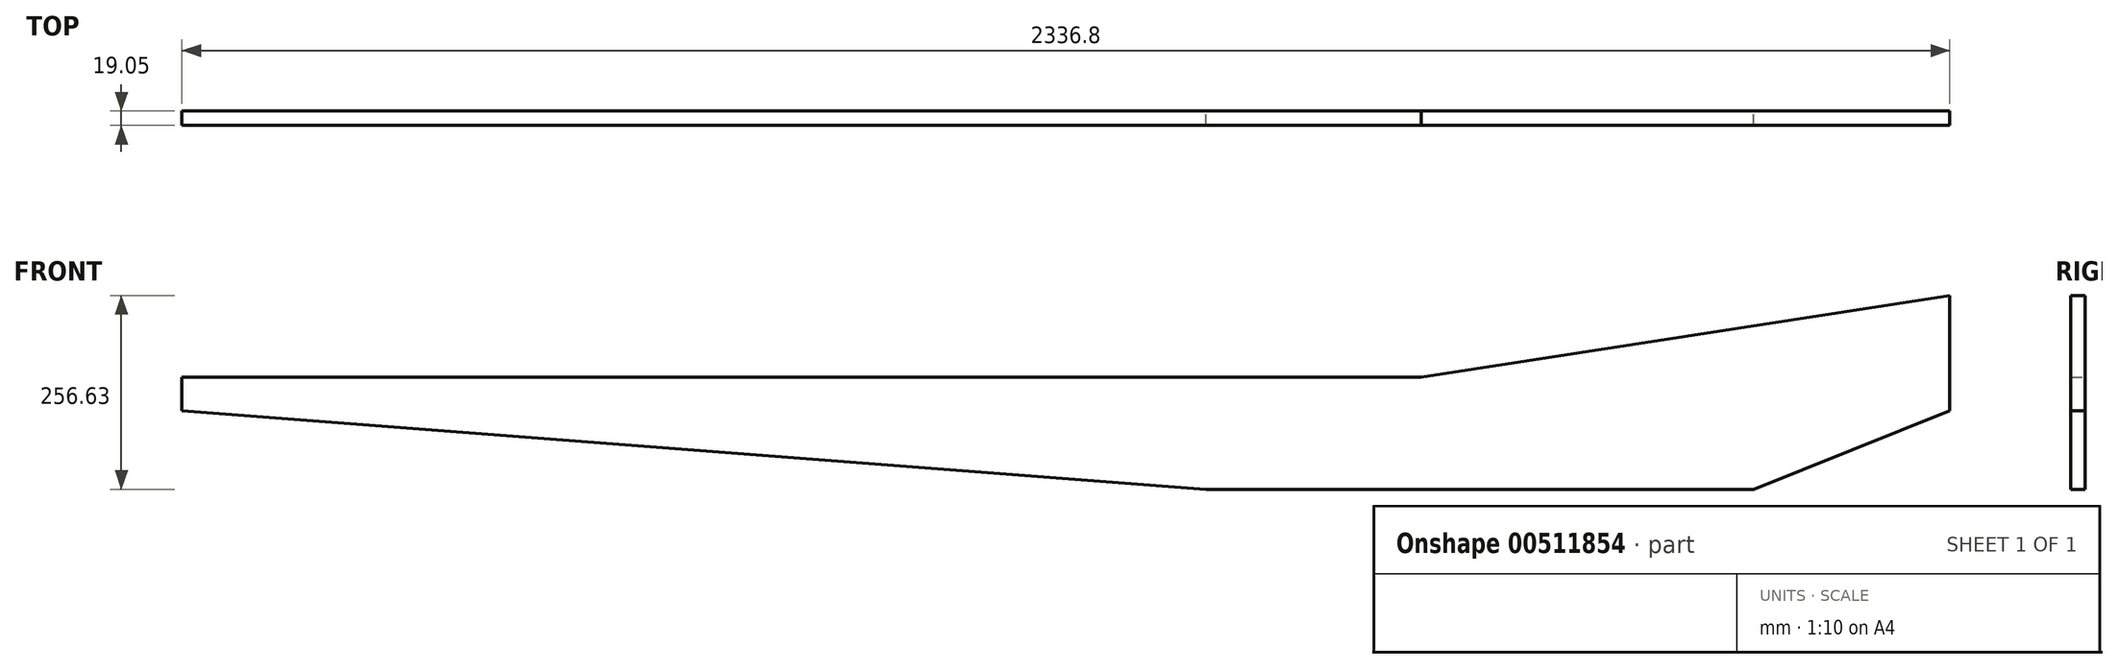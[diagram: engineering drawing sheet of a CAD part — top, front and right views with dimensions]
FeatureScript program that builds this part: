
annotation { "Feature Type Name" : "Feature", "Feature Type Description" : "" }
export const myFeature = defineFeature(function(context is Context, id is Id, definition is map)
    precondition{}
    {
        {
            var Q0;
            Q0=qCreatedBy(makeId("Front.planeOp"),FACE);
            var sketch = newSketch(context, id + "F0", { "sketchPlane" : qUnion([Q0])});
            skLineSegment(sketch, "E0", {"start": v(-1672.7, 71.47) * mm, "end": v(-34.4, 71.47) * mm});
            skLineSegment(sketch, "E1", {"start": v(-34.4, 71.47) * mm, "end": v(664.1, 179.42) * mm});
            skLineSegment(sketch, "E2", {"start": v(664.1, 179.42) * mm, "end": v(664.1, 27.02) * mm});
            skLineSegment(sketch, "E3", {"start": v(664.1, 27.02) * mm, "end": v(404.86, -77.2) * mm});
            skLineSegment(sketch, "E4", {"start": v(404.86, -77.2) * mm, "end": v(-319.04, -77.2) * mm});
            skLineSegment(sketch, "E5", {"start": v(-319.04, -77.2) * mm, "end": v(-1672.7, 27.02) * mm});
            skLineSegment(sketch, "E6", {"start": v(-1672.7, 27.02) * mm, "end": v(-1672.7, 71.47) * mm});
            skSolve(sketch);
        }
        {
            var Q0;
            Q0=makeQuery(id+"F0.imprint","IMPRINT",FACE,{"disambiguationData":[TD([[makeQuery(id+"F0.imprint","IMPRINT",EDGE,{"derivedFrom":sQuery(id+"F0.wireOp",EDGE,"E0")}),-1.0]])]});
            extrude(context, id + "F1", {"entities" : qUnion([Q0]), "depth" : 19.05 * mm});
        }
    });
